# Revit family: Grohe_FlushPlate_SpaPremium_104644KF00
name_source: partatom
category: Plumbing Fixtures
units: mm (PartAtom-declared; Revit-internal decimal feet)

## family parameters
Cut with Voids When Loaded = No
Host = Face
Maintain Annotation Orientation = No
Part Type = Normal
Room Calculation Point = No
Round Connector Dimension = Use Diameter
Shared = No

## types (1)
- SPA Flush Plate (104644KF00)
    AssetType = Fixed
    BIMObjectName = Grohe_FlushPlate_SpaPremium_104644KF00
    CO2NeutralProduction = GROHE is one of the first leading manufacturer within the sanitary industry having a CO2-neutral production.
    CW Connection = No
    ClassificationName = Uniclass2015
    ClassificationValue = Pr_75_50_46_31
    Color = Anthracite
    Cost = 0 $
    Default Elevation = 0 mm  [stored 0 ft]
    Description = SPA Flush Plate
    DimensionsDocumentLink = https://cdn.cloud.grohe.com
    DocumentationCertificates = https://www.bimstore.co
    DocumentationInstallationGuide = https://www.bimstore.co
    DocumentationLiterature = https://www.bimstore.co
    DocumentationMaintenance = https://www.bimstore.co
    DocumentationTechnical = https://www.bimstore.co
    DurationUnit = Years
    EF000007 = Anthracite
    EF000008 = 160
    EF000040 = 201
    EF001438 = 51
    EF002147 = Two button
    EF002169 = Plastic
    EF006331 = false
    EF006949 = Pneumatic
    EF010109 = false
    EF020827 = true
    EF020828 = false
    EF023751 = true
    EF023752 = true
    Ecojoy = No
    ExpectedLife = 0
    FullRecyclabilityOfPlastic = All plastic components are fully recycable
    GROHESocialCommittment = green.grohe.com/social_engagement
    GROHESustainability = green.grohe.com
    HW Connection = No
    IfcExportAs = IfcPipeFitting
    IfcExportType = IfcPipeFittingType
    Keynote = N13
    Manufacturer = Grohe
    ManufacturerName = Grohe
    Model = 104644KF00
    ModelNumber = 104644KF00
    ModelReference = SPA Flush Plate
    NBSDescription = Flush control devices
    NBSObjectName = Grohe - Flush control devices
    NBSReference = 90-15-35/470
    NominalDepth = 0 mm  [stored 0 ft]
    NominalHeight = 0 mm  [stored 0 ft]
    NominalLength = 0 mm  [stored 0 ft]
    PrimaryMaterial = Grohe_Anthracite
    ProductDescription = for dual flush actuation
for pneumatic discharge valve AV1
vertical installation
160 x 201 mm
material: ABS
GROHE Long-Life finish
GROHE Water Saving - Less water, perfect flow
for combination with Rapid SL and Uniset with GD 2 cistern, slim cistern and 80 mm cistern
compatible with auto flush of Sensia Arena, Sensia Pro and Hygiena
6 V lithium battery, type CR-P2
battery lifetime: 4 years for a 3 person household (approx. 17000 actuations)
battery status warning
auto flush
cleaning mode
for mains supply please order transformer 42 470 000
    ProductNumber = 104644KF00
    ProductShortText = Flush plate with soft touch actuation
    ProductionYear = 2024
    SustainabilityAward = green.grohe.com/awards
    SustainabilityReport = green.grohe.com/reporting
    TPIDocumentLink = https://cdn.cloud.grohe.com
    Type Comments = SPA Flush Plate
    TypeName = SPA Flush Plate
    URL = https://www.grohe.co.uk
    Vent Connection = No
    WarrantyDurationLabor = 0
    WarrantyDurationParts = 0
    WarrantyDurationUnit = Years
    Waste Connection = No
    _BSBibleVersion = 17
    _BimSpecGuid = 0
    _CurrentRevision = 1
    _DistributedBy = https://www.bimstore.co
    _ObjectUserGuide = https://www.bimstore.co

note: [stored X ft] marks values corroborated as IEEE doubles in the binary element streams (Revit-internal decimal feet)

## geometry (parser evidence)
native form markers: Sweep x3
no freeform markers — native parametric forms only
